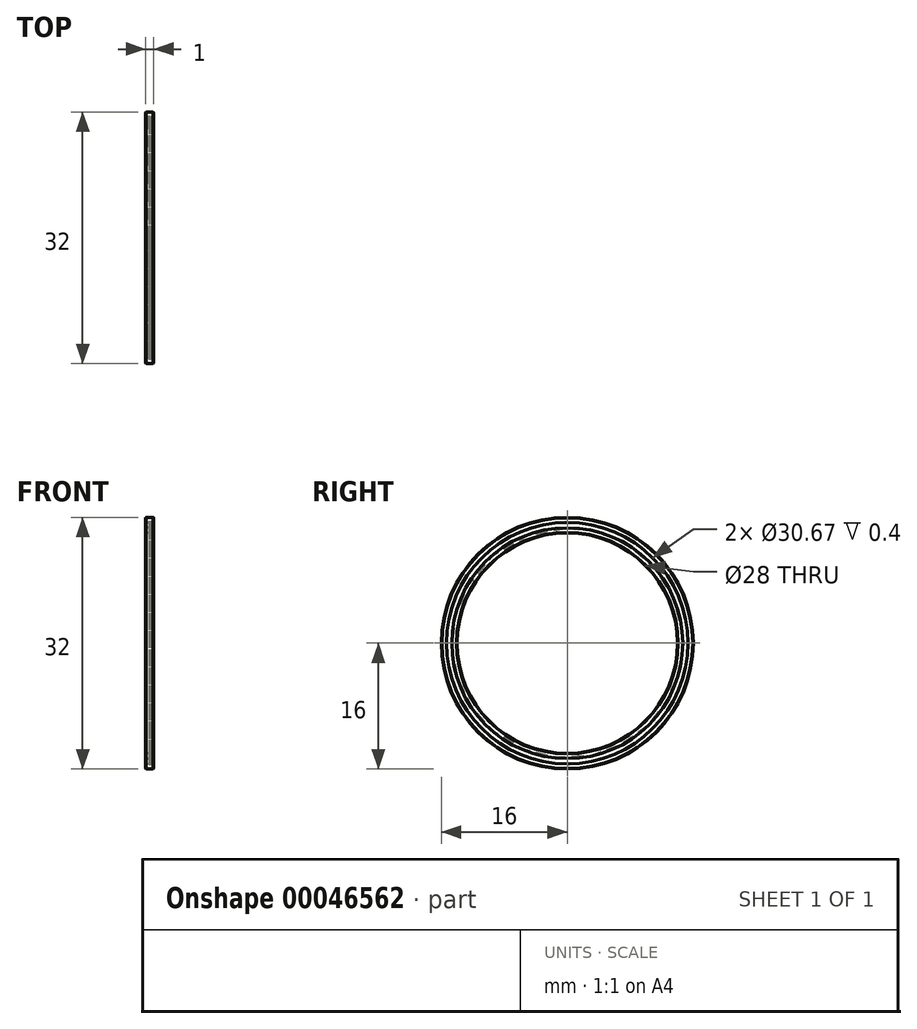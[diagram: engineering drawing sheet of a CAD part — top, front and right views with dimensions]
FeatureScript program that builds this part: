
annotation { "Feature Type Name" : "Feature", "Feature Type Description" : "" }
export const myFeature = defineFeature(function(context is Context, id is Id, definition is map)
    precondition{}
    {
        {
            assignVariable(context, id + "F0", {"name" : "W", "anyValue" : 1});
        }
        {
            var Q0;
            Q0=qCreatedBy(makeId("Front.planeOp"),FACE);
            var sketch = newSketch(context, id + "F1", { "sketchPlane" : qUnion([Q0])});
            skLineSegment(sketch, "E0.rect.bottom", {"start": v(0.5, 15.33) * mm, "end": v(0.1, 15.33) * mm});
            skLineSegment(sketch, "E0.rect.top", {"start": v(0.5, 16) * mm, "end": v(-0.5, 16) * mm});
            skLineSegment(sketch, "E0.rect.left", {"start": v(0.5, 15.33) * mm, "end": v(0.5, 16) * mm});
            skLineSegment(sketch, "E0.rect.right", {"start": v(-0.5, 15.33) * mm, "end": v(-0.5, 16) * mm});
            skPoint(sketch, "E0.rect.middle", {"position": v(0, 15.67) * mm});
            skLineSegment(sketch, "E1.rect.bottom", {"start": v(-0.5, 14.67) * mm, "end": v(-0.1, 14.67) * mm});
            skLineSegment(sketch, "E1.rect.top", {"start": v(-0.5, 14) * mm, "end": v(0.5, 14) * mm});
            skLineSegment(sketch, "E1.rect.left", {"start": v(-0.5, 14.67) * mm, "end": v(-0.5, 14) * mm});
            skLineSegment(sketch, "E1.rect.right", {"start": v(0.5, 14.67) * mm, "end": v(0.5, 14) * mm});
            skPoint(sketch, "E1.rect.middle", {"position": v(0, 14.33) * mm});
            skLineSegment(sketch, "E2", {"start": v(0, 15.33) * mm, "end": v(0, 14.67) * mm, "construction": true});
            skLineSegment(sketch, "E3", {"start": v(0, 15) * mm, "end": v(2, 15) * mm, "construction": true});
            skLineSegment(sketch, "E4.trimOffspring", {"start": v(-0.1, 15.33) * mm, "end": v(-0.5, 15.33) * mm});
            skLineSegment(sketch, "E5.trimOffspring", {"start": v(0.1, 14.67) * mm, "end": v(0.5, 14.67) * mm});
            skLineSegment(sketch, "E6", {"start": v(0, 0) * mm, "end": v(7.64, 0) * mm, "construction": true});
            skLineSegment(sketch, "E7", {"start": v(-0.1, 15.33) * mm, "end": v(-0.1, 14.67) * mm});
            skLineSegment(sketch, "E8", {"start": v(0.1, 15.33) * mm, "end": v(0.1, 14.67) * mm});
            skSolve(sketch);
        }
        {
            var Q0;
            Q0=qCreatedBy(makeId("Front.planeOp"),FACE);
            var sketch = newSketch(context, id + "F2", { "sketchPlane" : qUnion([Q0])});
            skCircle(sketch, "E9", {"center": v(0, 15) * mm, "radius": 0.4 * mm});
            skSolve(sketch);
        }
        {
            var Q0;
            Q0=makeQuery(id+"F1.imprint","IMPRINT",FACE,{"disambiguationData":[TD([[makeQuery(id+"F1.imprint","IMPRINT",EDGE,{"derivedFrom":sQuery(id+"F1.wireOp",EDGE,"E0.rect.bottom")}),-1.0]])]});
            var Q1;
            Q1=sQuery(id+"F1.wireOp",EDGE,"E6");
            revolve(context, id + "F3", {"entities" : qUnion([Q0]), "axis" : qUnion([Q1]), "revolveType" : RevolveType.FULL});
        }
        {
            var Q0;
            Q0 = qSketchRegion(id + "F2", true);
            var Q1;
            Q1=sQuery(id+"F1.wireOp",EDGE,"E6");
            revolve(context, id + "F4", {"entities" : qUnion([Q0]), "axis" : qUnion([Q1]), "revolveType" : RevolveType.FULL});
        }
        {
            var Q0;
            Q0=makeQuery(id+"F3.opRevolve","SWEPT_EDGE",EDGE,{"disambiguationData":[OSD([sQuery(id+"F1.wireOp",EDGE,"E0.rect.top"),sQuery(id+"F1.wireOp",EDGE,"E0.rect.right")])]});
            var Q1;
            Q1=makeQuery(id+"F3.opRevolve","SWEPT_EDGE",EDGE,{"disambiguationData":[OSD([sQuery(id+"F1.wireOp",EDGE,"E0.rect.top"),sQuery(id+"F1.wireOp",EDGE,"E0.rect.left")])]});
            var Q2;
            Q2=makeQuery(id+"F3.opRevolve","SWEPT_EDGE",EDGE,{"disambiguationData":[OSD([sQuery(id+"F1.wireOp",EDGE,"E1.rect.top"),sQuery(id+"F1.wireOp",EDGE,"E1.rect.right")])]});
            var Q3;
            Q3=makeQuery(id+"F3.opRevolve","SWEPT_EDGE",EDGE,{"disambiguationData":[OSD([sQuery(id+"F1.wireOp",EDGE,"E1.rect.top"),sQuery(id+"F1.wireOp",EDGE,"E1.rect.left")])]});
            chamfer(context, id + "F5", {"entities" : qUnion([Q0, Q1, Q2, Q3]), "width" : (getVariable(context, 'W') / 15) * mm, "tangentPropagation" : true});
        }
    });
